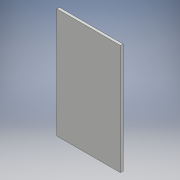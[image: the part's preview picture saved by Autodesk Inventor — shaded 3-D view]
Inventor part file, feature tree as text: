
AUTODESK INVENTOR PART (.ipt)
format: ipt  version: 2018 (Build 220112000, 112)  size: 89,600 bytes
history: native  units: mm
features: extrude x1, sketch x1
ambient origin geometry x8: Origin, YZ Plane, XZ Plane, XY Plane, X Axis, Y Axis, Z Axis, Center Point
bodies: Solid1 (feature_tree)
feature tree (2):
  extrude  "Extrusion1"  Depth=85.0mm
  sketch  "Sketch1"  dims[d0=49.0mm d1=85.0mm d2=2.0mm d3=0.0mm]
